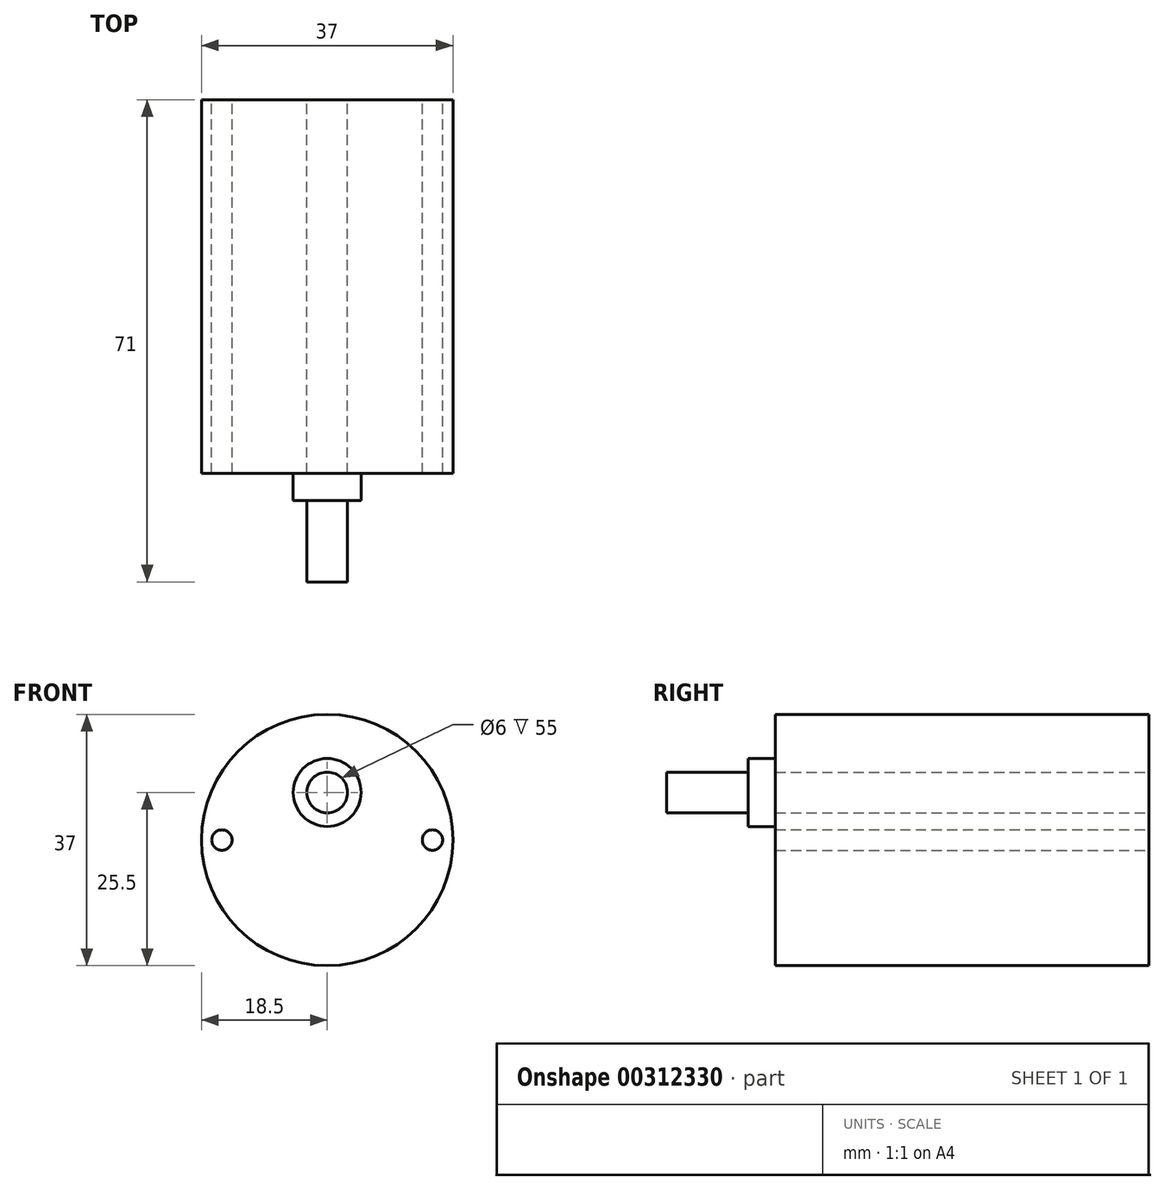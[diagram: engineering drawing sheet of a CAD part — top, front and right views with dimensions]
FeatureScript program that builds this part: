
annotation { "Feature Type Name" : "Feature", "Feature Type Description" : "" }
export const myFeature = defineFeature(function(context is Context, id is Id, definition is map)
    precondition{}
    {
        {
            var Q0;
            Q0=qCreatedBy(makeId("Front.planeOp"),FACE);
            var sketch = newSketch(context, id + "F0", { "sketchPlane" : qUnion([Q0])});
            skCircle(sketch, "E0", {"center": v(0, 0) * mm, "radius": 18.5 * mm});
            skLineSegment(sketch, "E1", {"start": v(-25.84, 0) * mm, "end": v(34.88, 0) * mm, "construction": true});
            skLineSegment(sketch, "E2", {"start": v(-37.64, 7) * mm, "end": v(37.64, 7) * mm, "construction": true});
            skCircle(sketch, "E3", {"center": v(0, 7) * mm, "radius": 3 * mm});
            skCircle(sketch, "E4", {"center": v(0, 0) * mm, "radius": 15.5 * mm, "construction": true});
            skCircle(sketch, "E5", {"center": v(15.5, 0) * mm, "radius": 1.5 * mm});
            skCircle(sketch, "E6", {"center": v(-15.5, 0) * mm, "radius": 1.5 * mm});
            skSolve(sketch);
        }
        {
            var Q0;
            Q0=qSketchRegion(id+"F0",true);
            extrude(context, id + "F1", {"entities" : qUnion([Q0]), "depth" : 55 * mm});
        }
        {
            var Q0;
            Q0=makeQuery(id+"F1.opExtrude","CAP_FACE",FACE,{"disambiguationData":[OSD([sQuery(id+"F0.wireOp",EDGE,"E0"),sQuery(id+"F0.wireOp",EDGE,"E3"),sQuery(id+"F0.wireOp",EDGE,"E5"),sQuery(id+"F0.wireOp",EDGE,"E6")])],"isStart":false});
            var sketch = newSketch(context, id + "F2", { "sketchPlane" : qUnion([Q0])});
            skCircle(sketch, "E7", {"center": v(0, 7) * mm, "radius": 5 * mm});
            skSolve(sketch);
        }
        {
            var Q0;
            Q0=qSketchRegion(id+"F2",true);
            extrude(context, id + "F3", {"entities" : qUnion([Q0]), "operationType" : NewBodyOperationType.ADD, "depth" : 4 * mm});
        }
        {
            var Q0;
            Q0=makeQuery(id+"F3.opExtrude","CAP_FACE",FACE,{"disambiguationData":[OSD([sQuery(id+"F2.wireOp",EDGE,"E7")])],"isStart":false});
            var sketch = newSketch(context, id + "F4", { "sketchPlane" : qUnion([Q0])});
            skCircle(sketch, "E8", {"center": v(0, 7) * mm, "radius": 3 * mm});
            skSolve(sketch);
        }
        {
            var Q0;
            Q0=qSketchRegion(id+"F4",true);
            extrude(context, id + "F5", {"entities" : qUnion([Q0]), "operationType" : NewBodyOperationType.ADD, "depth" : 12 * mm});
        }
    });
